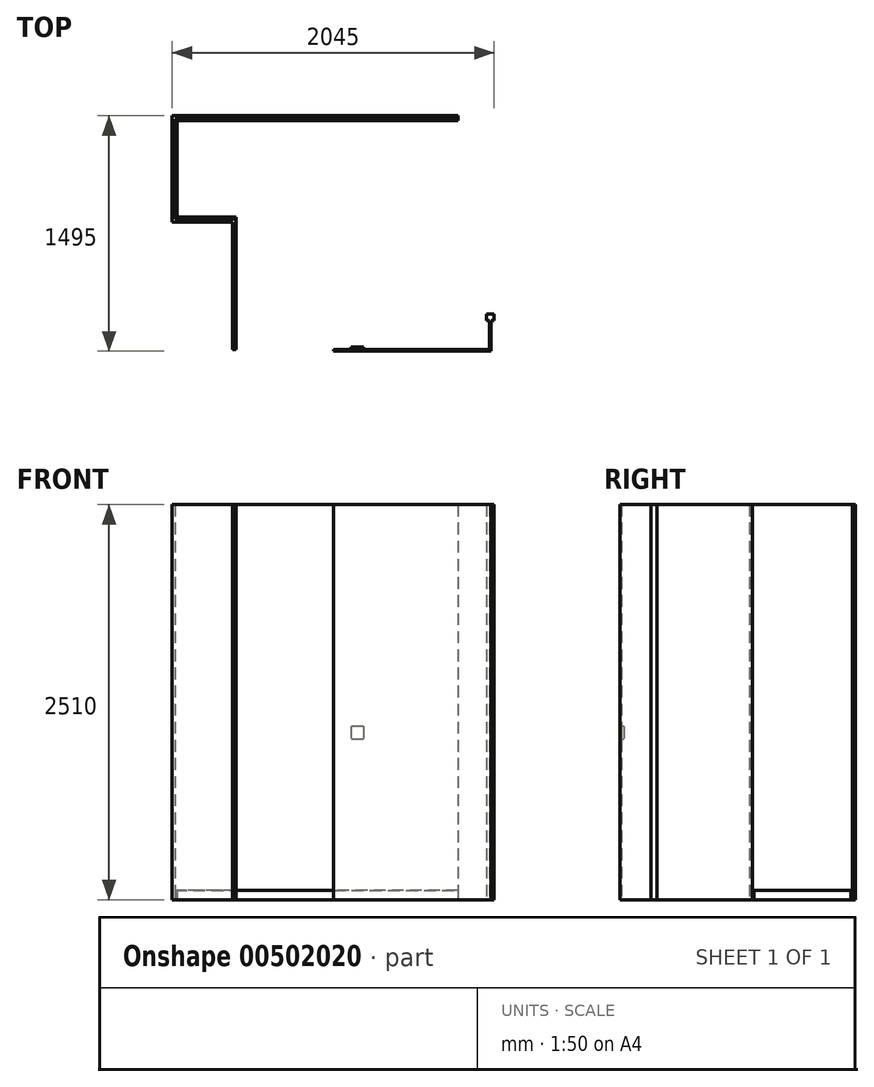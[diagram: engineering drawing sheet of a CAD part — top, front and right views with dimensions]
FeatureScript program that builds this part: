
annotation { "Feature Type Name" : "Feature", "Feature Type Description" : "" }
export const myFeature = defineFeature(function(context is Context, id is Id, definition is map)
    precondition{}
    {
        {
            var Q0;
            Q0=qCreatedBy(makeId("Top.planeOp"),FACE);
            var sketch = newSketch(context, id + "F0", { "sketchPlane" : qUnion([Q0])});
            skLineSegment(sketch, "E0", {"start": v(0, 0) * mm, "end": v(0, 830) * mm});
            skLineSegment(sketch, "E1", {"start": v(0, 830) * mm, "end": v(-385, 830) * mm});
            skLineSegment(sketch, "E2", {"start": v(-385, 830) * mm, "end": v(-385, 1465) * mm});
            skLineSegment(sketch, "E3", {"start": v(-385, 1465) * mm, "end": v(1410, 1465) * mm});
            skLineSegment(sketch, "E4", {"start": v(1410, 1465) * mm, "end": v(1410, 1485) * mm});
            skLineSegment(sketch, "E5", {"start": v(1410, 1485) * mm, "end": v(-405, 1485) * mm});
            skLineSegment(sketch, "E6", {"start": v(-405, 1485) * mm, "end": v(-405, 810) * mm});
            skLineSegment(sketch, "E7", {"start": v(-405, 810) * mm, "end": v(-20, 810) * mm});
            skLineSegment(sketch, "E8", {"start": v(-20, 810) * mm, "end": v(-20, 0) * mm});
            skLineSegment(sketch, "E9", {"start": v(-20, 0) * mm, "end": v(0, 0) * mm});
            skSolve(sketch);
        }
        {
            var Q0;
            Q0 = qSketchRegion(id + "F0", true);
            extrude(context, id + "F1", {"entities" : qUnion([Q0]), "depth" : 2510 * mm});
        }
        {
            var Q0;
            Q0=qCreatedBy(makeId("Top.planeOp"),FACE);
            var sketch = newSketch(context, id + "F2", { "sketchPlane" : qUnion([Q0])});
            skLineSegment(sketch, "E10", {"start": v(0, 840) * mm, "end": v(-375, 840) * mm});
            skLineSegment(sketch, "E11", {"start": v(-375, 840) * mm, "end": v(-375, 1455) * mm});
            skLineSegment(sketch, "E12", {"start": v(-375, 1455) * mm, "end": v(1410, 1455) * mm});
            skLineSegment(sketch, "E13", {"start": v(1410, 1455) * mm, "end": v(1410, 1465) * mm});
            skLineSegment(sketch, "E14", {"start": v(1410, 1465) * mm, "end": v(-385, 1465) * mm});
            skLineSegment(sketch, "E15", {"start": v(-385, 1465) * mm, "end": v(-385, 830) * mm});
            skLineSegment(sketch, "E16", {"start": v(-385, 830) * mm, "end": v(0, 830) * mm});
            skLineSegment(sketch, "E17", {"start": v(0, 830) * mm, "end": v(0, 840) * mm});
            skSolve(sketch);
        }
        {
            var Q0;
            Q0 = qSketchRegion(id + "F2", true);
            extrude(context, id + "F3", {"entities" : qUnion([Q0]), "depth" : 60 * mm});
        }
        {
            var Q0;
            Q0=qCreatedBy(makeId("Top.planeOp"),FACE);
            var sketch = newSketch(context, id + "F4", { "sketchPlane" : qUnion([Q0])});
            skLineSegment(sketch, "E18", {"start": v(1590, 225) * mm, "end": v(1640, 225) * mm});
            skLineSegment(sketch, "E19", {"start": v(1640, 225) * mm, "end": v(1640, 185) * mm});
            skLineSegment(sketch, "E20", {"start": v(1640, 185) * mm, "end": v(1620, 185) * mm});
            skLineSegment(sketch, "E21", {"start": v(1590, 185) * mm, "end": v(1590, 225) * mm});
            skLineSegment(sketch, "E22", {"start": v(1610, 185) * mm, "end": v(1610, 0) * mm});
            skLineSegment(sketch, "E23", {"start": v(1610, 0) * mm, "end": v(620, 0) * mm});
            skLineSegment(sketch, "E24", {"start": v(620, 0) * mm, "end": v(620, -10) * mm});
            skLineSegment(sketch, "E25", {"start": v(620, -10) * mm, "end": v(1620, -10) * mm});
            skLineSegment(sketch, "E26", {"start": v(1620, -10) * mm, "end": v(1620, 185) * mm});
            skLineSegment(sketch, "E27.trimOffspring", {"start": v(1610, 185) * mm, "end": v(1590, 185) * mm});
            skSolve(sketch);
        }
        {
            var Q0;
            Q0 = qSketchRegion(id + "F4", true);
            var Q1;
            Q1=makeQuery(id+"F1.opExtrude","CAP_FACE",FACE,{"disambiguationData":[OSD([sQuery(id+"F0.wireOp",EDGE,"E0"),sQuery(id+"F0.wireOp",EDGE,"E1"),sQuery(id+"F0.wireOp",EDGE,"E2"),sQuery(id+"F0.wireOp",EDGE,"E3"),sQuery(id+"F0.wireOp",EDGE,"E4"),sQuery(id+"F0.wireOp",EDGE,"E5"),sQuery(id+"F0.wireOp",EDGE,"E6"),sQuery(id+"F0.wireOp",EDGE,"E7"),sQuery(id+"F0.wireOp",EDGE,"E8"),sQuery(id+"F0.wireOp",EDGE,"E9")])],"isStart":false});
            extrude(context, id + "F5", {"entities" : qUnion([Q0]), "endBound" : BoundingType.UP_TO_SURFACE, "depth" : 25 * mm, "endBoundEntityFace" : qUnion([Q1]), "offsetDistance" : 25 * mm});
        }
        {
            var Q0;
            Q0=makeQuery(id+"F5.opExtrude","SWEPT_FACE",FACE,{"disambiguationData":[OSD([sQuery(id+"F4.wireOp",EDGE,"E23")])]});
            var sketch = newSketch(context, id + "F6", { "sketchPlane" : qUnion([Q0])});
            skLineSegment(sketch, "E28.bottom", {"start": v(-810, 1100) * mm, "end": v(-730, 1100) * mm});
            skLineSegment(sketch, "E28.top", {"start": v(-810, 1020) * mm, "end": v(-730, 1020) * mm});
            skLineSegment(sketch, "E28.left", {"start": v(-810, 1100) * mm, "end": v(-810, 1020) * mm});
            skLineSegment(sketch, "E28.right", {"start": v(-730, 1100) * mm, "end": v(-730, 1020) * mm});
            skSolve(sketch);
        }
        {
            var Q0;
            Q0 = qSketchRegion(id + "F6", true);
            extrude(context, id + "F7", {"entities" : qUnion([Q0]), "operationType" : NewBodyOperationType.ADD, "depth" : 15 * mm, "offsetDistance" : 25 * mm});
        }
    });
